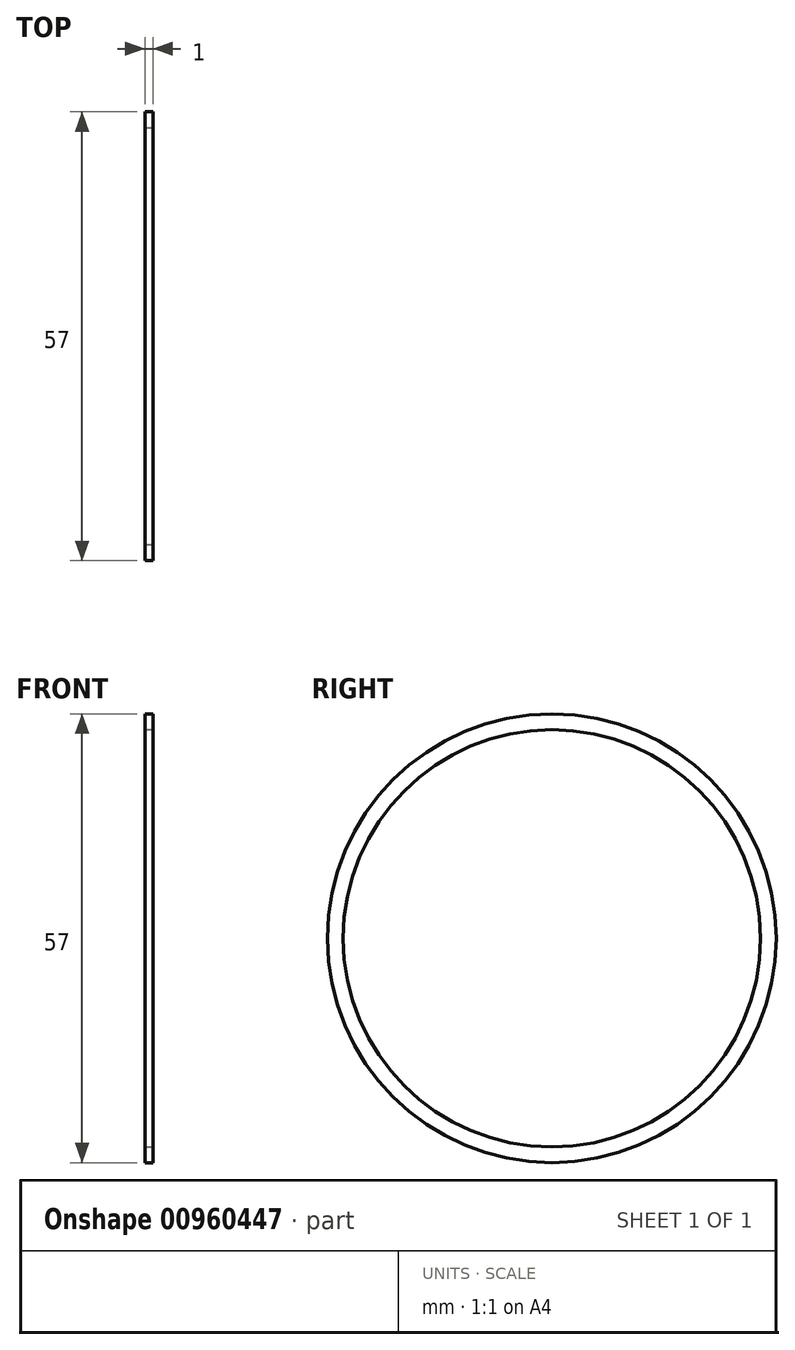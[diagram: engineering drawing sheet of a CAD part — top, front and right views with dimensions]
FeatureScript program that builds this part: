
annotation { "Feature Type Name" : "Feature", "Feature Type Description" : "" }
export const myFeature = defineFeature(function(context is Context, id is Id, definition is map)
    precondition{}
    {
        {
            var Q0;
            Q0=qCreatedBy(makeId("Front.planeOp"),FACE);
            var sketch = newSketch(context, id + "F0", { "sketchPlane" : qUnion([Q0])});
            skLineSegment(sketch, "E0.bottom", {"start": v(-14.02, 28.5) * mm, "end": v(-15.02, 28.5) * mm});
            skLineSegment(sketch, "E0.top", {"start": v(-14.02, 26.5) * mm, "end": v(-15.02, 26.5) * mm});
            skLineSegment(sketch, "E0.left", {"start": v(-14.02, 28.5) * mm, "end": v(-14.02, 26.5) * mm});
            skLineSegment(sketch, "E0.right", {"start": v(-15.02, 28.5) * mm, "end": v(-15.02, 26.5) * mm});
            skLineSegment(sketch, "E1", {"start": v(0, 0) * mm, "end": v(-14.12, 0) * mm});
            skSolve(sketch);
        }
        {
            var Q0;
            Q0=qSketchRegion(id+"F0",true);
            var Q1;
            Q1=sQuery(id+"F0.wireOp",EDGE,"E1");
            revolve(context, id + "F1", {"surfaceOperationType" : NewSurfaceOperationType.NEW, "entities" : qUnion([Q0]), "axis" : qUnion([Q1]), "revolveType" : RevolveType.FULL});
        }
    });
